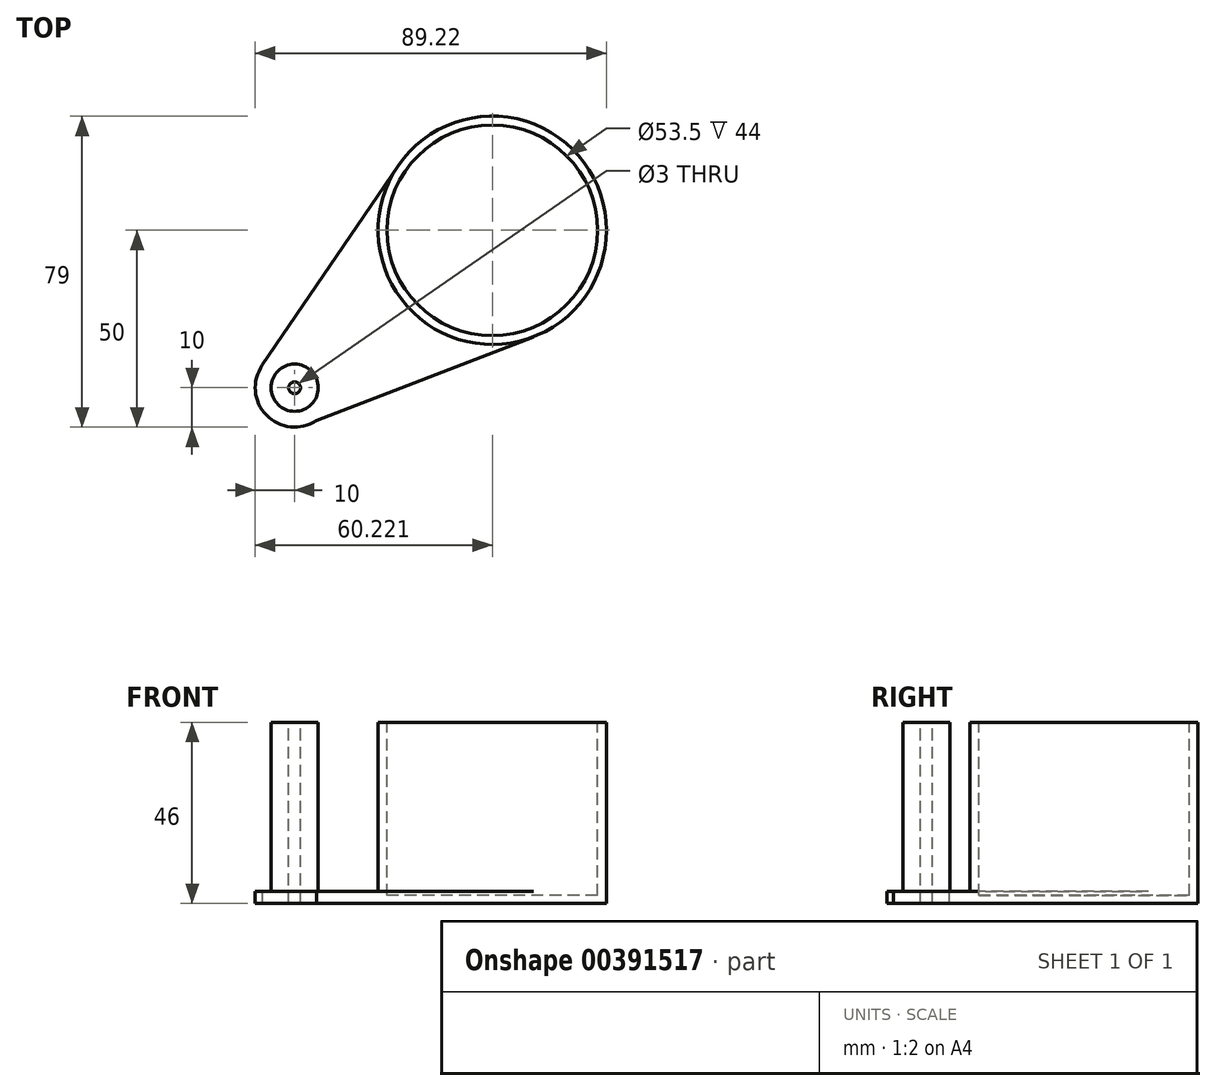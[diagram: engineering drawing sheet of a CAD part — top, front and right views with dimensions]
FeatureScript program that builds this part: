
annotation { "Feature Type Name" : "Feature", "Feature Type Description" : "" }
export const myFeature = defineFeature(function(context is Context, id is Id, definition is map)
    precondition{}
    {
        {
            var Q0;
            Q0=qCreatedBy(makeId("Top.planeOp"),FACE);
            var sketch = newSketch(context, id + "F0", { "sketchPlane" : qUnion([Q0])});
            skArc(sketch, "E0", {"start": v(88.16, 12.95) * mm, "mid": v(100.44, 58.02) * mm, "end": v(53.75, 56.32) * mm});
            skArc(sketch, "E1", {"start": v(19.3, 5.71) * mm, "mid": v(20.34, -6.99) * mm, "end": v(33.01, -8.34) * mm});
            skLineSegment(sketch, "E2", {"start": v(33.01, -8.34) * mm, "end": v(88.16, 12.95) * mm});
            skLineSegment(sketch, "E3", {"start": v(19.3, 5.71) * mm, "end": v(53.75, 56.32) * mm});
            skSolve(sketch);
        }
        {
            var Q0;
            Q0 = qSketchRegion(id + "F0", true);
            extrude(context, id + "F1", {"entities" : qUnion([Q0]), "depth" : 3 * mm});
        }
        {
            var Q0;
            Q0=makeQuery(id+"F1.opExtrude","CAP_FACE",FACE,{"disambiguationData":[OSD([sQuery(id+"F0.wireOp",EDGE,"E0"),sQuery(id+"F0.wireOp",EDGE,"E1"),sQuery(id+"F0.wireOp",EDGE,"E2"),sQuery(id+"F0.wireOp",EDGE,"E3")])],"isStart":false});
            var sketch = newSketch(context, id + "F2", { "sketchPlane" : qUnion([Q0])});
            skCircle(sketch, "E4", {"center": v(27.5, 0) * mm, "radius": 6 * mm});
            skCircle(sketch, "E5", {"center": v(77.72, 40) * mm, "radius": 29 * mm});
            skSolve(sketch);
        }
        {
            var Q0;
            Q0 = qSketchRegion(id + "F2", true);
            extrude(context, id + "F3", {"entities" : qUnion([Q0]), "operationType" : NewBodyOperationType.ADD, "depth" : 43 * mm});
        }
        {
            var Q0;
            Q0=makeQuery(id+"F3.opExtrude","CAP_FACE",FACE,{"disambiguationData":[OSD([sQuery(id+"F2.wireOp",EDGE,"E5")])],"isStart":false});
            var sketch = newSketch(context, id + "F4", { "sketchPlane" : qUnion([Q0])});
            skCircle(sketch, "E6", {"center": v(77.72, 40) * mm, "radius": 26.75 * mm});
            skSolve(sketch);
        }
        {
            var Q0;
            Q0 = qSketchRegion(id + "F4", true);
            var Q1;
            Q1 = qSketchRegion(id + "F6", true);
            extrude(context, id + "F5", {"entities" : qUnion([Q0, Q1]), "operationType" : NewBodyOperationType.REMOVE, "oppositeDirection" : true, "depth" : 44 * mm});
        }
        {
            var Q0;
            Q0=makeQuery(id+"F3.opExtrude","CAP_FACE",FACE,{"disambiguationData":[OSD([sQuery(id+"F2.wireOp",EDGE,"E4")])],"isStart":false});
            var sketch = newSketch(context, id + "F6", { "sketchPlane" : qUnion([Q0])});
            skCircle(sketch, "E7", {"center": v(27.5, 0) * mm, "radius": 1.5 * mm});
            skSolve(sketch);
        }
        {
            var Q0;
            Q0 = qSketchRegion(id + "F6", true);
            extrude(context, id + "F7", {"entities" : qUnion([Q0]), "operationType" : NewBodyOperationType.REMOVE, "oppositeDirection" : true, "depth" : 47 * mm});
        }
    });
